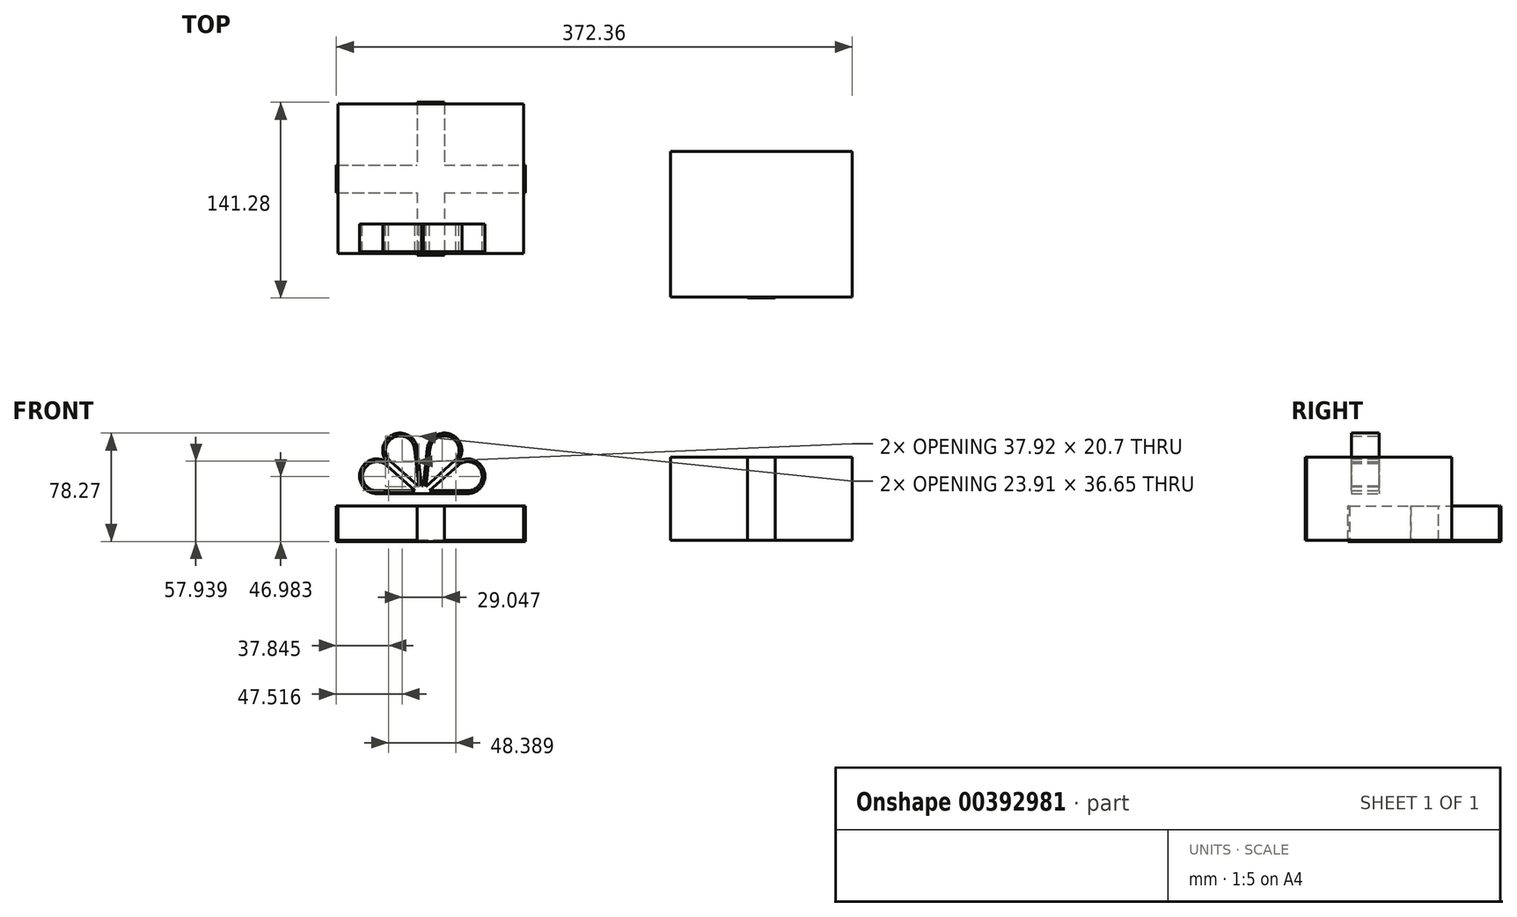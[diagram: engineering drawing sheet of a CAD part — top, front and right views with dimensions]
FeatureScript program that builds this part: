
annotation { "Feature Type Name" : "Feature", "Feature Type Description" : "" }
export const myFeature = defineFeature(function(context is Context, id is Id, definition is map)
    precondition{}
    {
        {
            var Q0;
            Q0=qCreatedBy(makeId("Top.planeOp"),FACE);
            var sketch = newSketch(context, id + "F0", { "sketchPlane" : qUnion([Q0])});
            skLineSegment(sketch, "E0.bottom", {"start": v(-65.5, -52.5) * mm, "end": v(65.5, -52.5) * mm});
            skLineSegment(sketch, "E0.top", {"start": v(-65.5, 52.5) * mm, "end": v(65.5, 52.5) * mm});
            skLineSegment(sketch, "E0.left", {"start": v(-65.5, -52.5) * mm, "end": v(-65.5, 52.5) * mm});
            skLineSegment(sketch, "E0.right", {"start": v(65.5, -52.5) * mm, "end": v(65.5, 52.5) * mm});
            skPoint(sketch, "E0.middle", {"position": v(0, 0) * mm});
            skLineSegment(sketch, "E1.bottom", {"start": v(-171.66, -21.22) * mm, "end": v(-305.66, -21.22) * mm});
            skLineSegment(sketch, "E1.top", {"start": v(-171.66, 86.78) * mm, "end": v(-305.66, 86.78) * mm});
            skLineSegment(sketch, "E1.left", {"start": v(-171.66, -21.22) * mm, "end": v(-171.66, 86.78) * mm});
            skLineSegment(sketch, "E1.right", {"start": v(-305.66, -21.22) * mm, "end": v(-305.66, 86.78) * mm});
            skPoint(sketch, "E1.middle", {"position": v(-238.66, 32.78) * mm});
            skLineSegment(sketch, "E2.bottom", {"start": v(-306.86, 22.78) * mm, "end": v(-170.46, 22.78) * mm});
            skLineSegment(sketch, "E2.top", {"start": v(-306.86, 42.78) * mm, "end": v(-170.46, 42.78) * mm});
            skLineSegment(sketch, "E2.left", {"start": v(-306.86, 22.78) * mm, "end": v(-306.86, 42.78) * mm});
            skLineSegment(sketch, "E2.right", {"start": v(-170.46, 22.78) * mm, "end": v(-170.46, 42.78) * mm});
            skLineSegment(sketch, "E3.bottom", {"start": v(-248.66, 87.98) * mm, "end": v(-228.66, 87.98) * mm});
            skLineSegment(sketch, "E3.top", {"start": v(-248.66, -22.42) * mm, "end": v(-228.66, -22.42) * mm});
            skLineSegment(sketch, "E3.left", {"start": v(-248.66, 87.98) * mm, "end": v(-248.66, -22.42) * mm});
            skLineSegment(sketch, "E3.right", {"start": v(-228.66, 87.98) * mm, "end": v(-228.66, -22.42) * mm});
            skLineSegment(sketch, "E4", {"start": v(-228.66, 87.18) * mm, "end": v(-248.66, 87.18) * mm});
            skLineSegment(sketch, "E5", {"start": v(-248.66, -21.62) * mm, "end": v(-228.66, -21.62) * mm});
            skLineSegment(sketch, "E6", {"start": v(-306.06, 42.78) * mm, "end": v(-306.06, 22.78) * mm});
            skLineSegment(sketch, "E7", {"start": v(-171.26, 42.78) * mm, "end": v(-171.26, 22.78) * mm});
            skSolve(sketch);
        }
        {
            var Q0;
            Q0=makeQuery(id+"F0.imprint","IMPRINT",FACE,{"disambiguationData":[TD([[makeQuery(id+"F0.imprint","IMPRINT",EDGE,{"derivedFrom":sQuery(id+"F0.wireOp",EDGE,"E0.bottom")}),1.0]])]});
            extrude(context, id + "F1", {"entities" : qUnion([Q0]), "depth" : 60 * mm});
        }
        {
            var Q0;
            Q0=makeQuery(id+"F0.imprint","IMPRINT",FACE,{"disambiguationData":[TD([[makeQuery(id+"F0.imprint","IMPRINT",EDGE,{"derivedFrom":sQuery(id+"F0.wireOp",EDGE,"E0.bottom")}),1.0]])]});
            var Q1;
            {var subQ0=sQuery(id+"F0.wireOp",EDGE,"E1.left");var subQ1=sQuery(id+"F0.wireOp",EDGE,"E1.bottom");var subQ2=makeQuery(id+"F0.imprint","INTERSECT",VERTEX,{"derivedFrom":[subQ1,subQ0]});Q1=makeQuery(id+"F0.imprint","IMPRINT",FACE,{"disambiguationData":[TD([[makeQuery(id+"F0.imprint","IMPRINT",EDGE,{"disambiguationData":[TD([[subQ2,-1.0]])],"derivedFrom":subQ1}),-1.0]])]});}
            var Q2;
            {var subQ0=sQuery(id+"F0.wireOp",EDGE,"E1.right");var subQ1=sQuery(id+"F0.wireOp",EDGE,"E1.bottom");var subQ2=makeQuery(id+"F0.imprint","INTERSECT",VERTEX,{"derivedFrom":[subQ1,subQ0]});Q2=makeQuery(id+"F0.imprint","IMPRINT",FACE,{"disambiguationData":[TD([[makeQuery(id+"F0.imprint","IMPRINT",EDGE,{"disambiguationData":[TD([[subQ2,1.0]])],"derivedFrom":subQ1}),-1.0]])]});}
            var Q3;
            {var subQ0=sQuery(id+"F0.wireOp",EDGE,"E1.left");var subQ1=sQuery(id+"F0.wireOp",EDGE,"E1.top");var subQ2=makeQuery(id+"F0.imprint","INTERSECT",VERTEX,{"derivedFrom":[subQ1,subQ0]});Q3=makeQuery(id+"F0.imprint","IMPRINT",FACE,{"disambiguationData":[TD([[makeQuery(id+"F0.imprint","IMPRINT",EDGE,{"disambiguationData":[TD([[subQ2,-1.0]])],"derivedFrom":subQ1}),1.0]])]});}
            var Q4;
            {var subQ0=sQuery(id+"F0.wireOp",EDGE,"E1.right");var subQ1=sQuery(id+"F0.wireOp",EDGE,"E1.top");var subQ2=makeQuery(id+"F0.imprint","INTERSECT",VERTEX,{"derivedFrom":[subQ1,subQ0]});Q4=makeQuery(id+"F0.imprint","IMPRINT",FACE,{"disambiguationData":[TD([[makeQuery(id+"F0.imprint","IMPRINT",EDGE,{"disambiguationData":[TD([[subQ2,1.0]])],"derivedFrom":subQ1}),1.0]])]});}
            var Q5;
            {var subQ0=sQuery(id+"F0.wireOp",EDGE,"E3.right");var subQ1=sQuery(id+"F0.wireOp",EDGE,"E1.bottom");var subQ2=makeQuery(id+"F0.imprint","INTERSECT",VERTEX,{"derivedFrom":[subQ1,subQ0]});Q5=makeQuery(id+"F0.imprint","IMPRINT",FACE,{"disambiguationData":[TD([[makeQuery(id+"F0.imprint","IMPRINT",EDGE,{"disambiguationData":[TD([[subQ2,-1.0]])],"derivedFrom":subQ1}),-1.0]])]});}
            var Q6;
            {var subQ0=sQuery(id+"F0.wireOp",EDGE,"E3.right");var subQ1=sQuery(id+"F0.wireOp",EDGE,"E1.top");var subQ2=makeQuery(id+"F0.imprint","INTERSECT",VERTEX,{"derivedFrom":[subQ1,subQ0]});Q6=makeQuery(id+"F0.imprint","IMPRINT",FACE,{"disambiguationData":[TD([[makeQuery(id+"F0.imprint","IMPRINT",EDGE,{"disambiguationData":[TD([[subQ2,-1.0]])],"derivedFrom":subQ1}),1.0]])]});}
            var Q7;
            {var subQ0=sQuery(id+"F0.wireOp",EDGE,"E2.bottom");var subQ1=sQuery(id+"F0.wireOp",EDGE,"E1.left");var subQ2=makeQuery(id+"F0.imprint","INTERSECT",VERTEX,{"derivedFrom":[subQ1,subQ0]});Q7=makeQuery(id+"F0.imprint","IMPRINT",FACE,{"disambiguationData":[TD([[makeQuery(id+"F0.imprint","IMPRINT",EDGE,{"disambiguationData":[TD([[subQ2,-1.0]])],"derivedFrom":subQ1}),1.0]])]});}
            var Q8;
            {var subQ0=sQuery(id+"F0.wireOp",EDGE,"E2.bottom");var subQ1=sQuery(id+"F0.wireOp",EDGE,"E1.right");var subQ2=makeQuery(id+"F0.imprint","INTERSECT",VERTEX,{"derivedFrom":[subQ1,subQ0]});Q8=makeQuery(id+"F0.imprint","IMPRINT",FACE,{"disambiguationData":[TD([[makeQuery(id+"F0.imprint","IMPRINT",EDGE,{"disambiguationData":[TD([[subQ2,-1.0]])],"derivedFrom":subQ1}),-1.0]])]});}
            var Q9;
            {var subQ0=sQuery(id+"F0.wireOp",EDGE,"E3.left");var subQ1=sQuery(id+"F0.wireOp",EDGE,"E2.bottom");var subQ2=makeQuery(id+"F0.imprint","INTERSECT",VERTEX,{"derivedFrom":[subQ1,subQ0]});Q9=makeQuery(id+"F0.imprint","IMPRINT",FACE,{"disambiguationData":[TD([[makeQuery(id+"F0.imprint","IMPRINT",EDGE,{"disambiguationData":[TD([[subQ2,-1.0]])],"derivedFrom":subQ1}),1.0]])]});}
            extrude(context, id + "F2", {"entities" : qUnion([Q0, Q1, Q2, Q3, Q4, Q5, Q6, Q7, Q8, Q9]), "operationType" : NewBodyOperationType.ADD, "depth" : 25 * mm});
        }
        {
            var Q0;
            {var subQ0=sQuery(id+"F0.wireOp",EDGE,"E2.left");Q0=makeQuery(id+"F0.imprint","IMPRINT",FACE,{"disambiguationData":[TD([[makeQuery(id+"F0.imprint","IMPRINT",EDGE,{"derivedFrom":subQ0}),-1.0]])]});}
            var Q1;
            {var subQ5=sQuery(id+"F0.wireOp",EDGE,"E6");Q1=makeQuery(id+"F0.imprint","IMPRINT",FACE,{"disambiguationData":[TD([[makeQuery(id+"F0.imprint","IMPRINT",EDGE,{"derivedFrom":subQ5}),1.0]])]});}
            var Q2;
            {var subQ0=sQuery(id+"F0.wireOp",EDGE,"E2.bottom");var subQ1=sQuery(id+"F0.wireOp",EDGE,"E1.right");var subQ2=makeQuery(id+"F0.imprint","INTERSECT",VERTEX,{"derivedFrom":[subQ1,subQ0]});Q2=makeQuery(id+"F0.imprint","IMPRINT",FACE,{"disambiguationData":[TD([[makeQuery(id+"F0.imprint","IMPRINT",EDGE,{"disambiguationData":[TD([[subQ2,-1.0]])],"derivedFrom":subQ1}),-1.0]])]});}
            var Q3;
            {var subQ5=sQuery(id+"F0.wireOp",EDGE,"E7");Q3=makeQuery(id+"F0.imprint","IMPRINT",FACE,{"disambiguationData":[TD([[makeQuery(id+"F0.imprint","IMPRINT",EDGE,{"derivedFrom":subQ5}),-1.0]])]});}
            var Q4;
            {var subQ0=sQuery(id+"F0.wireOp",EDGE,"E2.right");Q4=makeQuery(id+"F0.imprint","IMPRINT",FACE,{"disambiguationData":[TD([[makeQuery(id+"F0.imprint","IMPRINT",EDGE,{"derivedFrom":subQ0}),1.0]])]});}
            var Q5;
            {var subQ0=sQuery(id+"F0.wireOp",EDGE,"E3.bottom");Q5=makeQuery(id+"F0.imprint","IMPRINT",FACE,{"disambiguationData":[TD([[makeQuery(id+"F0.imprint","IMPRINT",EDGE,{"derivedFrom":subQ0}),-1.0]])]});}
            var Q6;
            {var subQ5=sQuery(id+"F0.wireOp",EDGE,"E4");Q6=makeQuery(id+"F0.imprint","IMPRINT",FACE,{"disambiguationData":[TD([[makeQuery(id+"F0.imprint","IMPRINT",EDGE,{"derivedFrom":subQ5}),1.0]])]});}
            var Q7;
            {var subQ5=sQuery(id+"F0.wireOp",EDGE,"E5");Q7=makeQuery(id+"F0.imprint","IMPRINT",FACE,{"disambiguationData":[TD([[makeQuery(id+"F0.imprint","IMPRINT",EDGE,{"derivedFrom":subQ5}),1.0]])]});}
            var Q8;
            {var subQ0=sQuery(id+"F0.wireOp",EDGE,"E3.top");Q8=makeQuery(id+"F0.imprint","IMPRINT",FACE,{"disambiguationData":[TD([[makeQuery(id+"F0.imprint","IMPRINT",EDGE,{"derivedFrom":subQ0}),1.0]])]});}
            var Q9;
            {var subQ0=sQuery(id+"F0.wireOp",EDGE,"E3.left");var subQ1=sQuery(id+"F0.wireOp",EDGE,"E2.bottom");var subQ2=makeQuery(id+"F0.imprint","INTERSECT",VERTEX,{"derivedFrom":[subQ1,subQ0]});Q9=makeQuery(id+"F0.imprint","IMPRINT",FACE,{"disambiguationData":[TD([[makeQuery(id+"F0.imprint","IMPRINT",EDGE,{"disambiguationData":[TD([[subQ2,-1.0]])],"derivedFrom":subQ1}),1.0]])]});}
            var Q10;
            {var subQ0=sQuery(id+"F0.wireOp",EDGE,"E2.bottom");var subQ1=sQuery(id+"F0.wireOp",EDGE,"E1.left");var subQ2=makeQuery(id+"F0.imprint","INTERSECT",VERTEX,{"derivedFrom":[subQ1,subQ0]});Q10=makeQuery(id+"F0.imprint","IMPRINT",FACE,{"disambiguationData":[TD([[makeQuery(id+"F0.imprint","IMPRINT",EDGE,{"disambiguationData":[TD([[subQ2,-1.0]])],"derivedFrom":subQ1}),1.0]])]});}
            var Q11;
            {var subQ0=sQuery(id+"F0.wireOp",EDGE,"E3.right");var subQ1=sQuery(id+"F0.wireOp",EDGE,"E1.top");var subQ2=makeQuery(id+"F0.imprint","INTERSECT",VERTEX,{"derivedFrom":[subQ1,subQ0]});Q11=makeQuery(id+"F0.imprint","IMPRINT",FACE,{"disambiguationData":[TD([[makeQuery(id+"F0.imprint","IMPRINT",EDGE,{"disambiguationData":[TD([[subQ2,-1.0]])],"derivedFrom":subQ1}),1.0]])]});}
            var Q12;
            {var subQ0=sQuery(id+"F0.wireOp",EDGE,"E3.right");var subQ1=sQuery(id+"F0.wireOp",EDGE,"E1.bottom");var subQ2=makeQuery(id+"F0.imprint","INTERSECT",VERTEX,{"derivedFrom":[subQ1,subQ0]});Q12=makeQuery(id+"F0.imprint","IMPRINT",FACE,{"disambiguationData":[TD([[makeQuery(id+"F0.imprint","IMPRINT",EDGE,{"disambiguationData":[TD([[subQ2,-1.0]])],"derivedFrom":subQ1}),-1.0]])]});}
            extrude(context, id + "F3", {"entities" : qUnion([Q0, Q1, Q2, Q3, Q4, Q5, Q6, Q7, Q8, Q9, Q10, Q11, Q12]), "oppositeDirection" : true, "depth" : .8 * mm});
        }
        {
            var Q0;
            {var subQ0=sQuery(id+"F0.wireOp",EDGE,"E2.left");Q0=makeQuery(id+"F0.imprint","IMPRINT",FACE,{"disambiguationData":[TD([[makeQuery(id+"F0.imprint","IMPRINT",EDGE,{"derivedFrom":subQ0}),-1.0]])]});}
            var Q1;
            {var subQ0=sQuery(id+"F0.wireOp",EDGE,"E3.bottom");Q1=makeQuery(id+"F0.imprint","IMPRINT",FACE,{"disambiguationData":[TD([[makeQuery(id+"F0.imprint","IMPRINT",EDGE,{"derivedFrom":subQ0}),-1.0]])]});}
            var Q2;
            {var subQ0=sQuery(id+"F0.wireOp",EDGE,"E2.right");Q2=makeQuery(id+"F0.imprint","IMPRINT",FACE,{"disambiguationData":[TD([[makeQuery(id+"F0.imprint","IMPRINT",EDGE,{"derivedFrom":subQ0}),1.0]])]});}
            var Q3;
            {var subQ0=sQuery(id+"F0.wireOp",EDGE,"E3.top");Q3=makeQuery(id+"F0.imprint","IMPRINT",FACE,{"disambiguationData":[TD([[makeQuery(id+"F0.imprint","IMPRINT",EDGE,{"derivedFrom":subQ0}),1.0]])]});}
            extrude(context, id + "F4", {"entities" : qUnion([Q0, Q1, Q2, Q3]), "operationType" : NewBodyOperationType.ADD, "depth" : 25 * mm});
        }
        {
            var Q0;
            Q0=makeQuery(id+"F1.opExtrude","SWEPT_FACE",FACE,{"disambiguationData":[OSD([sQuery(id+"F0.wireOp",EDGE,"E0.bottom")])]});
            var sketch = newSketch(context, id + "F5", { "sketchPlane" : qUnion([Q0])});
            skLineSegment(sketch, "E8.bottom", {"start": v(-10, 0) * mm, "end": v(10, 0) * mm});
            skLineSegment(sketch, "E8.top", {"start": v(-10, 130) * mm, "end": v(10, 130) * mm});
            skLineSegment(sketch, "E8.left", {"start": v(-10, 0) * mm, "end": v(-10, 130) * mm});
            skLineSegment(sketch, "E8.right", {"start": v(10, 0) * mm, "end": v(10, 130) * mm});
            skSolve(sketch);
        }
        {
            var Q0;
            Q0=makeQuery(id+"F5.imprint","IMPRINT",FACE,{"disambiguationData":[TD([[makeQuery(id+"F5.imprint","IMPRINT",EDGE,{"derivedFrom":sQuery(id+"F5.wireOp",EDGE,"E8.bottom")}),1.0]])]});
            extrude(context, id + "F6", {"entities" : qUnion([Q0]), "depth" : .8 * mm});
        }
        {
            var Q0;
            Q0=qCreatedBy(makeId("Front.planeOp"),FACE);
            var sketch = newSketch(context, id + "F7", { "sketchPlane" : qUnion([Q0])});
            skArc(sketch, "E9", {"start": v(-269.21, 55.65) * mm, "mid": v(-289.23, 50.8) * mm, "end": v(-277.55, 33.83) * mm});
            skArc(sketch, "E10", {"start": v(-212.1, 33.83) * mm, "mid": v(-200.42, 50.8) * mm, "end": v(-220.43, 55.65) * mm});
            skArc(sketch, "E11", {"start": v(-248.46, 66.36) * mm, "mid": v(-266.61, 76.08) * mm, "end": v(-269.21, 55.65) * mm});
            skArc(sketch, "E12", {"start": v(-220.43, 55.65) * mm, "mid": v(-223.03, 76.08) * mm, "end": v(-241.18, 66.36) * mm});
            skLineSegment(sketch, "E13", {"start": v(-244.82, 33.83) * mm, "end": v(-248.46, 66.36) * mm});
            skLineSegment(sketch, "E14", {"start": v(-244.82, 33.83) * mm, "end": v(-269.21, 55.65) * mm});
            skLineSegment(sketch, "E15", {"start": v(-244.82, 33.83) * mm, "end": v(-241.18, 66.36) * mm});
            skLineSegment(sketch, "E16", {"start": v(-244.82, 33.83) * mm, "end": v(-220.43, 55.65) * mm});
            skLineSegment(sketch, "E17.0", {"start": v(-242.25, 38.81) * mm, "end": v(-239.2, 66.13) * mm});
            skLineSegment(sketch, "E17.1", {"start": v(-242.25, 38.81) * mm, "end": v(-221.76, 57.14) * mm});
            skArc(sketch, "E17.2", {"start": v(-221.76, 57.14) * mm, "mid": v(-223.95, 74.3) * mm, "end": v(-239.2, 66.13) * mm});
            skLineSegment(sketch, "E18.0", {"start": v(-247.4, 38.81) * mm, "end": v(-250.45, 66.13) * mm});
            skLineSegment(sketch, "E18.1", {"start": v(-247.4, 38.81) * mm, "end": v(-267.88, 57.14) * mm});
            skArc(sketch, "E18.2", {"start": v(-250.45, 66.13) * mm, "mid": v(-265.7, 74.3) * mm, "end": v(-267.88, 57.14) * mm});
            skLineSegment(sketch, "E19", {"start": v(-277.55, 33.83) * mm, "end": v(-244.82, 33.83) * mm});
            skLineSegment(sketch, "E20", {"start": v(-212.1, 33.83) * mm, "end": v(-244.82, 33.83) * mm});
            skLineSegment(sketch, "E21.0", {"start": v(-250.06, 35.83) * mm, "end": v(-270.55, 54.16) * mm});
            skLineSegment(sketch, "E21.1", {"start": v(-277.55, 35.83) * mm, "end": v(-250.06, 35.83) * mm});
            skArc(sketch, "E21.2", {"start": v(-270.55, 54.16) * mm, "mid": v(-287.36, 50.08) * mm, "end": v(-277.55, 35.83) * mm});
            skLineSegment(sketch, "E22.0", {"start": v(-239.58, 35.83) * mm, "end": v(-219.1, 54.16) * mm});
            skLineSegment(sketch, "E22.1", {"start": v(-212.1, 35.83) * mm, "end": v(-239.58, 35.83) * mm});
            skArc(sketch, "E22.2", {"start": v(-212.1, 35.83) * mm, "mid": v(-202.28, 50.08) * mm, "end": v(-219.1, 54.16) * mm});
            skArc(sketch, "E23", {"start": v(-239.22, 33.83) * mm, "mid": v(-244.82, 39.44) * mm, "end": v(-250.43, 33.83) * mm});
            skSolve(sketch);
        }
        {
            var Q0;
            {var subQ1=sQuery(id+"F7.wireOp",EDGE,"E9");Q0=makeQuery(id+"F7.imprint","IMPRINT",FACE,{"disambiguationData":[TD([[makeQuery(id+"F7.imprint","IMPRINT",EDGE,{"derivedFrom":subQ1}),1.0]])]});}
            var Q1;
            {var subQ1=sQuery(id+"F7.wireOp",EDGE,"E14");var subQ3=sQuery(id+"F7.wireOp",EDGE,"E23");var subQ4=makeQuery(id+"F7.imprint","INTERSECT",VERTEX,{"derivedFrom":[subQ1,subQ3]});Q1=makeQuery(id+"F7.imprint","IMPRINT",FACE,{"disambiguationData":[TD([[makeQuery(id+"F7.imprint","IMPRINT",EDGE,{"disambiguationData":[TD([[subQ4,-1.0]])],"derivedFrom":subQ3}),1.0]])]});}
            var Q2;
            {var subQ1=sQuery(id+"F7.wireOp",EDGE,"E13");var subQ3=sQuery(id+"F7.wireOp",EDGE,"E23");var subQ4=makeQuery(id+"F7.imprint","INTERSECT",VERTEX,{"derivedFrom":[subQ1,subQ3]});Q2=makeQuery(id+"F7.imprint","IMPRINT",FACE,{"disambiguationData":[TD([[makeQuery(id+"F7.imprint","IMPRINT",EDGE,{"disambiguationData":[TD([[subQ4,-1.0]])],"derivedFrom":subQ3}),1.0]])]});}
            var Q3;
            {var subQ2=sQuery(id+"F7.wireOp",EDGE,"E11");Q3=makeQuery(id+"F7.imprint","IMPRINT",FACE,{"disambiguationData":[TD([[makeQuery(id+"F7.imprint","IMPRINT",EDGE,{"derivedFrom":subQ2}),1.0]])]});}
            var Q4;
            {var subQ2=sQuery(id+"F7.wireOp",EDGE,"E12");Q4=makeQuery(id+"F7.imprint","IMPRINT",FACE,{"disambiguationData":[TD([[makeQuery(id+"F7.imprint","IMPRINT",EDGE,{"derivedFrom":subQ2}),1.0]])]});}
            var Q5;
            {var subQ0=sQuery(id+"F7.wireOp",EDGE,"E16");var subQ3=sQuery(id+"F7.wireOp",EDGE,"E23");var subQ5=makeQuery(id+"F7.imprint","INTERSECT",VERTEX,{"derivedFrom":[subQ0,subQ3]});Q5=makeQuery(id+"F7.imprint","IMPRINT",FACE,{"disambiguationData":[TD([[makeQuery(id+"F7.imprint","IMPRINT",EDGE,{"disambiguationData":[TD([[subQ5,-1.0]])],"derivedFrom":subQ3}),1.0]])]});}
            var Q6;
            {var subQ1=sQuery(id+"F7.wireOp",EDGE,"E13");var subQ3=sQuery(id+"F7.wireOp",EDGE,"E23");var subQ4=makeQuery(id+"F7.imprint","INTERSECT",VERTEX,{"derivedFrom":[subQ1,subQ3]});Q6=makeQuery(id+"F7.imprint","IMPRINT",FACE,{"disambiguationData":[TD([[makeQuery(id+"F7.imprint","IMPRINT",EDGE,{"disambiguationData":[TD([[subQ4,1.0]])],"derivedFrom":subQ3}),1.0]])]});}
            var Q7;
            {var subQ0=sQuery(id+"F7.wireOp",EDGE,"E20");var subQ3=sQuery(id+"F7.wireOp",EDGE,"E23");var subQ5=makeQuery(id+"F7.imprint","INTERSECT",VERTEX,{"derivedFrom":[subQ0,subQ3]});Q7=makeQuery(id+"F7.imprint","IMPRINT",FACE,{"disambiguationData":[TD([[makeQuery(id+"F7.imprint","IMPRINT",EDGE,{"disambiguationData":[TD([[subQ5,-1.0]])],"derivedFrom":subQ3}),1.0]])]});}
            var Q8;
            {var subQ2=sQuery(id+"F7.wireOp",EDGE,"E10");Q8=makeQuery(id+"F7.imprint","IMPRINT",FACE,{"disambiguationData":[TD([[makeQuery(id+"F7.imprint","IMPRINT",EDGE,{"derivedFrom":subQ2}),1.0]])]});}
            extrude(context, id + "F8", {"entities" : qUnion([Q0, Q1, Q2, Q3, Q4, Q5, Q6, Q7, Q8]), "depth" : 20 * mm});
        }
    });
